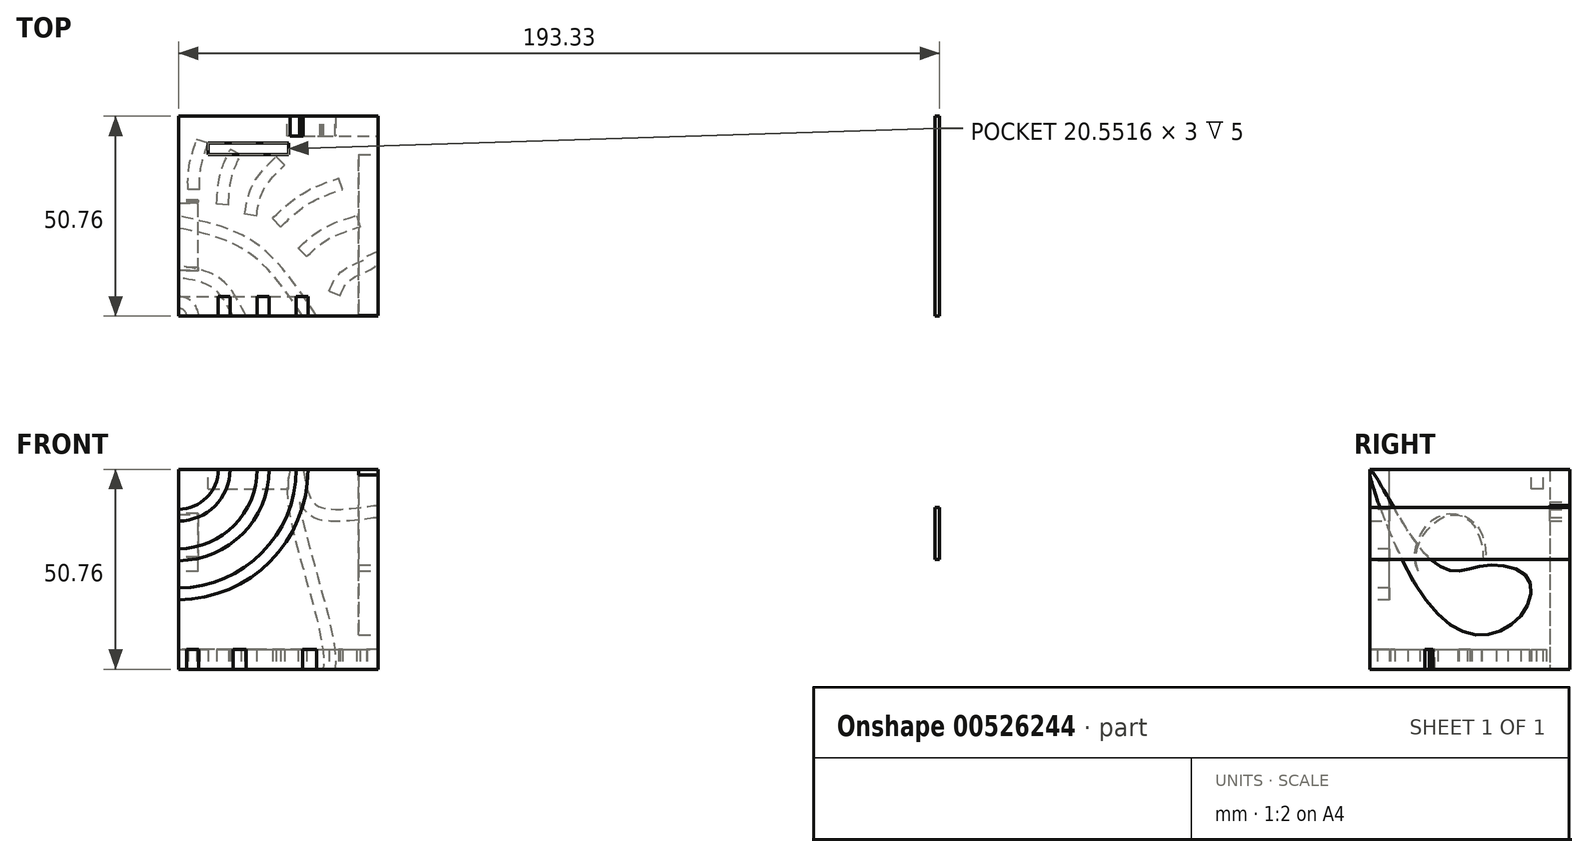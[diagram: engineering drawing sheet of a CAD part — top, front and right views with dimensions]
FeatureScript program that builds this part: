
annotation { "Feature Type Name" : "Feature", "Feature Type Description" : "" }
export const myFeature = defineFeature(function(context is Context, id is Id, definition is map)
    precondition{}
    {
        {
            var Q0;
            Q0=qCreatedBy(makeId("Front.planeOp"),FACE);
            var sketch = newSketch(context, id + "F0", { "sketchPlane" : qUnion([Q0])});
            skLineSegment(sketch, "E0.bottom", {"start": v(-59.56, 56.89) * mm, "end": v(-8.8, 56.89) * mm});
            skLineSegment(sketch, "E0.top", {"start": v(-59.56, 6.13) * mm, "end": v(-8.8, 6.13) * mm});
            skLineSegment(sketch, "E0.left", {"start": v(-59.56, 56.89) * mm, "end": v(-59.56, 6.13) * mm});
            skLineSegment(sketch, "E0.right", {"start": v(-8.8, 56.89) * mm, "end": v(-8.8, 6.13) * mm});
            skLineSegment(sketch, "E1.bottom", {"start": v(133.77, 47.2) * mm, "end": v(132.63, 47.2) * mm});
            skLineSegment(sketch, "E1.top", {"start": v(133.77, 38.64) * mm, "end": v(132.63, 38.64) * mm});
            skLineSegment(sketch, "E1.left", {"start": v(133.77, 47.2) * mm, "end": v(133.77, 38.64) * mm});
            skLineSegment(sketch, "E1.right", {"start": v(132.63, 47.2) * mm, "end": v(132.63, 38.64) * mm});
            skLineSegment(sketch, "E2.bottom", {"start": v(132.63, 38.64) * mm, "end": v(133.77, 38.64) * mm});
            skLineSegment(sketch, "E2.top", {"start": v(132.63, 34.08) * mm, "end": v(133.77, 34.08) * mm});
            skLineSegment(sketch, "E2.left", {"start": v(132.63, 38.64) * mm, "end": v(132.63, 34.08) * mm});
            skLineSegment(sketch, "E2.right", {"start": v(133.77, 38.64) * mm, "end": v(133.77, 34.08) * mm});
            skSolve(sketch);
        }
        {
            var Q0;
            Q0=qSketchRegion(id+"F0",true);
            extrude(context, id + "F1", {"entities" : qUnion([Q0]), "depth" : 50.76 * mm, "offsetDistance" : 25 * mm});
        }
        {
            var Q0;
            Q0=makeQuery(id+"F1.opExtrude","CAP_FACE",FACE,{"disambiguationData":[OSD([sQuery(id+"F0.wireOp",EDGE,"E0.bottom"),sQuery(id+"F0.wireOp",EDGE,"E0.top"),sQuery(id+"F0.wireOp",EDGE,"E0.left"),sQuery(id+"F0.wireOp",EDGE,"E0.right")])],"isStart":false});
            var sketch = newSketch(context, id + "F2", { "sketchPlane" : qUnion([Q0])});
            skSolve(sketch);
        }
        {
            var Q0;
            Q0=makeQuery(id+"F2.imprint","IMPRINT",FACE,{"disambiguationData":[TD([[makeQuery(id+"F2.imprint","IMPRINT",EDGE,{"derivedFrom":makeQuery(id+"F1.opExtrude","CAP_EDGE",EDGE,{"disambiguationData":[OSD([sQuery(id+"F0.wireOp",EDGE,"E0.bottom")])],"isStart":false})}),-1.0]])]});
            var sketch = newSketch(context, id + "F3", { "sketchPlane" : qUnion([Q0])});
            skArc(sketch, "E3", {"start": v(-59.55, 46.8) * mm, "mid": v(-52.35, 49.82) * mm, "end": v(-49.46, 57.07) * mm});
            skArc(sketch, "E4.0", {"start": v(-59.55, 43.8) * mm, "mid": v(-50.21, 47.72) * mm, "end": v(-46.46, 57.13) * mm});
            skLineSegment(sketch, "E5", {"start": v(-59.55, 46.8) * mm, "end": v(-64.57, 43.8) * mm});
            skLineSegment(sketch, "E6", {"start": v(-64.57, 43.8) * mm, "end": v(-59.55, 43.8) * mm});
            skLineSegment(sketch, "E7", {"start": v(-49.46, 57.07) * mm, "end": v(-46.79, 60.64) * mm});
            skLineSegment(sketch, "E8", {"start": v(-46.79, 60.64) * mm, "end": v(-46.46, 57.13) * mm});
            skSolve(sketch);
        }
        {
            var Q0;
            Q0=makeQuery(id+"F2.imprint","IMPRINT",FACE,{"disambiguationData":[TD([[makeQuery(id+"F2.imprint","IMPRINT",EDGE,{"derivedFrom":makeQuery(id+"F1.opExtrude","CAP_EDGE",EDGE,{"disambiguationData":[OSD([sQuery(id+"F0.wireOp",EDGE,"E0.bottom")])],"isStart":false})}),-1.0]])]});
            var sketch = newSketch(context, id + "F4", { "sketchPlane" : qUnion([Q0])});
            skArc(sketch, "E9", {"start": v(-59.74, 36.71) * mm, "mid": v(-45.4, 42.69) * mm, "end": v(-39.56, 57.08) * mm});
            skArc(sketch, "E10", {"start": v(-59.74, 26.81) * mm, "mid": v(-38.47, 35.62) * mm, "end": v(-29.66, 56.9) * mm});
            skArc(sketch, "E11.0", {"start": v(-59.74, 23.81) * mm, "mid": v(-36.35, 33.5) * mm, "end": v(-26.66, 56.9) * mm});
            skArc(sketch, "E12.0", {"start": v(-59.74, 33.71) * mm, "mid": v(-43.27, 40.58) * mm, "end": v(-36.56, 57.1) * mm});
            skLineSegment(sketch, "E13", {"start": v(-59.74, 36.71) * mm, "end": v(-64.36, 33.9) * mm});
            skLineSegment(sketch, "E14", {"start": v(-64.36, 33.9) * mm, "end": v(-59.74, 33.71) * mm});
            skLineSegment(sketch, "E15", {"start": v(-59.74, 26.81) * mm, "end": v(-63.86, 25.48) * mm});
            skLineSegment(sketch, "E16", {"start": v(-63.86, 25.48) * mm, "end": v(-59.74, 23.81) * mm});
            skLineSegment(sketch, "E17", {"start": v(-39.56, 57.08) * mm, "end": v(-36.56, 63.03) * mm});
            skLineSegment(sketch, "E18", {"start": v(-36.56, 63.03) * mm, "end": v(-36.56, 57.1) * mm});
            skLineSegment(sketch, "E19", {"start": v(-29.66, 56.9) * mm, "end": v(-26.66, 64.32) * mm});
            skLineSegment(sketch, "E20", {"start": v(-26.66, 64.32) * mm, "end": v(-26.66, 56.9) * mm});
            skSolve(sketch);
        }
        {
            var Q0;
            Q0=makeQuery(id+"F1.opExtrude","SWEPT_FACE",FACE,{"disambiguationData":[OSD([sQuery(id+"F0.wireOp",EDGE,"E0.bottom")])]});
            var sketch = newSketch(context, id + "F5", { "sketchPlane" : qUnion([Q0])});
            skLineSegment(sketch, "E21", {"start": v(-52.08, -6.76) * mm, "end": v(-31.52, -6.76) * mm});
            skLineSegment(sketch, "E22.0", {"start": v(-52.08, -9.76) * mm, "end": v(-31.52, -9.76) * mm});
            skLineSegment(sketch, "E23", {"start": v(-52.08, -6.76) * mm, "end": v(-52.08, -9.76) * mm});
            skLineSegment(sketch, "E24", {"start": v(-31.52, -6.76) * mm, "end": v(-31.52, -9.76) * mm});
            skSolve(sketch);
        }
        {
            var Q0;
            Q0=qCreatedBy(makeId("Front.planeOp"),FACE);
            var sketch = newSketch(context, id + "F6", { "sketchPlane" : qUnion([Q0])});
            skFitSpline(sketch, "E25", {"points": [v(-31.15, 57.08) * mm, v(-31.71, 47.74) * mm, v(-23.3, 13.73) * mm, v(-22.93, 6.26) * mm, v(-23.12, 6.26) * mm], "startDerivative": vector(-6.9, -29.17) * mm, "endDerivative": vector(-5.47, 1.83) * mm});
            skFitSpline(sketch, "E26.0", {"points": [v(-28.23, 56.39) * mm, v(-28.38, 55.78) * mm, v(-28.64, 54.64) * mm, v(-28.87, 53.23) * mm, v(-28.96, 51.94) * mm, v(-28.97, 50.87) * mm, v(-28.91, 49.65) * mm, v(-28.8, 48.5) * mm, v(-28.64, 47.46) * mm, v(-28.46, 46.35) * mm, v(-28.17, 44.85) * mm, v(-27.73, 42.87) * mm, v(-27.05, 40.06) * mm, v(-26.06, 36.27) * mm, v(-24.73, 31.48) * mm, v(-23.37, 26.65) * mm, v(-22.3, 22.72) * mm, v(-21.54, 19.72) * mm, v(-21.03, 17.56) * mm, v(-20.58, 15.52) * mm, v(-20.22, 13.6) * mm, v(-19.96, 11.83) * mm, v(-19.81, 10.52) * mm, v(-19.74, 9.56) * mm, v(-19.7, 8.9) * mm, v(-19.68, 8.27) * mm, v(-19.68, 7.7) * mm, v(-19.7, 7.16) * mm, v(-19.73, 6.74) * mm, v(-19.77, 6.4) * mm, v(-19.8, 6.15) * mm, v(-19.87, 5.87) * mm, v(-19.95, 5.57) * mm, v(-20.07, 5.22) * mm, v(-20.25, 4.84) * mm, v(-20.5, 4.48) * mm, v(-20.72, 4.22) * mm, v(-20.95, 4) * mm, v(-21.23, 3.78) * mm, v(-21.64, 3.53) * mm, v(-22.17, 3.33) * mm, v(-22.69, 3.24) * mm, v(-23.13, 3.23) * mm, v(-23.6, 3.28) * mm, v(-23.95, 3.37) * mm, v(-24.05, 3.4) * mm, v(-24.07, 3.41) * mm]});
            skLineSegment(sketch, "E27", {"start": v(-31.15, 57.08) * mm, "end": v(-27.86, 64.5) * mm});
            skLineSegment(sketch, "E28", {"start": v(-27.86, 64.5) * mm, "end": v(-28.23, 56.39) * mm});
            skLineSegment(sketch, "E29", {"start": v(-33.73, 3.41) * mm, "end": v(-24.07, 3.41) * mm});
            skLineSegment(sketch, "E30", {"start": v(-23.12, 6.26) * mm, "end": v(-33.73, 3.41) * mm});
            skSolve(sketch);
        }
        {
            var Q0;
            Q0=makeQuery(id+"F1.opExtrude","CAP_FACE",FACE,{"disambiguationData":[OSD([sQuery(id+"F0.wireOp",EDGE,"E0.bottom"),sQuery(id+"F0.wireOp",EDGE,"E0.top"),sQuery(id+"F0.wireOp",EDGE,"E0.left"),sQuery(id+"F0.wireOp",EDGE,"E0.right")])],"isStart":true});
            var sketch = newSketch(context, id + "F7", { "sketchPlane" : qUnion([Q0])});
            skFitSpline(sketch, "E31", {"points": [v(30.94, 56.89) * mm, v(24.23, 44.4) * mm, v(8.8, 44.68) * mm, v(8.8, 44.4) * mm], "startDerivative": vector(-5.85, -35.55) * mm, "endDerivative": vector(2.46, -5.15) * mm});
            skFitSpline(sketch, "E32.0", {"points": [v(27.98, 57.37) * mm, v(27.85, 56.63) * mm, v(27.62, 55.18) * mm, v(27.22, 53.16) * mm, v(26.73, 51.37) * mm, v(26.14, 49.87) * mm, v(25.45, 48.74) * mm, v(24.81, 48.07) * mm, v(24.22, 47.66) * mm, v(23.7, 47.4) * mm, v(23.08, 47.17) * mm, v(22.28, 46.99) * mm, v(21.33, 46.86) * mm, v(19.92, 46.77) * mm, v(18.36, 46.79) * mm, v(16.75, 46.9) * mm, v(15.56, 47) * mm, v(14.4, 47.14) * mm, v(13.28, 47.28) * mm, v(12.42, 47.4) * mm, v(11.77, 47.48) * mm, v(11.31, 47.54) * mm, v(10.87, 47.6) * mm, v(10.46, 47.65) * mm, v(10.07, 47.69) * mm, v(9.7, 47.72) * mm, v(9.37, 47.73) * mm, v(9.1, 47.74) * mm, v(8.87, 47.73) * mm, v(8.6, 47.7) * mm, v(8.33, 47.66) * mm, v(8.06, 47.6) * mm, v(7.82, 47.52) * mm, v(7.53, 47.4) * mm, v(7.2, 47.22) * mm, v(6.83, 46.96) * mm, v(6.47, 46.6) * mm, v(6.16, 46.17) * mm, v(5.93, 45.68) * mm, v(5.8, 45.2) * mm, v(5.72, 44.62) * mm, v(5.77, 44.05) * mm, v(5.89, 43.61) * mm, v(6, 43.34) * mm, v(6.07, 43.18) * mm, v(6.1, 43.12) * mm, v(6.1, 43.1) * mm]});
            skLineSegment(sketch, "E33", {"start": v(27.98, 57.37) * mm, "end": v(30.94, 56.89) * mm});
            skLineSegment(sketch, "E34", {"start": v(8.8, 44.68) * mm, "end": v(6.1, 43.1) * mm});
            skSolve(sketch);
        }
        {
            var Q0;
            Q0=makeQuery(id+"F1.opExtrude","SWEPT_FACE",FACE,{"disambiguationData":[OSD([sQuery(id+"F0.wireOp",EDGE,"E0.top")])]});
            var sketch = newSketch(context, id + "F8", { "sketchPlane" : qUnion([Q0])});
            skFitSpline(sketch, "E35", {"points": [v(-42.36, 50.76) * mm, v(-49.09, 41.2) * mm, v(-59.56, 38.02) * mm], "startDerivative": vector(-11.18, -21.96) * mm, "endDerivative": vector(-23.28, -3.42) * mm});
            skFitSpline(sketch, "E36", {"points": [v(-24.42, 50.76) * mm, v(-40.3, 32.04) * mm, v(-59.56, 25.38) * mm], "startDerivative": vector(-27.72, -41.47) * mm, "endDerivative": vector(-42.78, -8.78) * mm});
            skFitSpline(sketch, "E37", {"points": [v(-21.25, 44.37) * mm, v(-17.7, 39.14) * mm, v(-11.72, 35.97) * mm, v(-11.72, 35.6) * mm], "startDerivative": vector(5.24, -12.88) * mm, "endDerivative": vector(-1.53, -3.26) * mm});
            skFitSpline(sketch, "E38", {"points": [v(-27.04, 35.7) * mm, v(-21.62, 31.3) * mm, v(-13.4, 28.12) * mm], "startDerivative": vector(10.55, -10.16) * mm, "endDerivative": vector(16.6, -5.11) * mm});
            skFitSpline(sketch, "E39", {"points": [v(-33.58, 28.12) * mm, v(-26.67, 22.33) * mm, v(-17.89, 18.59) * mm], "startDerivative": vector(13.21, -12.83) * mm, "endDerivative": vector(18.15, -6.26) * mm});
            skFitSpline(sketch, "E40", {"points": [v(-39.75, 25.38) * mm, v(-37.88, 18.59) * mm, v(-32.65, 12.42) * mm], "startDerivative": vector(2.36, -14.58) * mm, "endDerivative": vector(11.73, -11.36) * mm});
            skFitSpline(sketch, "E41", {"points": [v(-46.84, 22.51) * mm, v(-45.91, 15.04) * mm, v(-43.67, 9.8) * mm], "startDerivative": vector(0.92, -14.7) * mm, "endDerivative": vector(5.54, -10.62) * mm});
            skFitSpline(sketch, "E42", {"points": [v(-54.13, 18.59) * mm, v(-53.94, 13.55) * mm, v(-52.08, 6.82) * mm], "startDerivative": vector(-0.3, -10.64) * mm, "endDerivative": vector(4.28, -12.84) * mm});
            skFitSpline(sketch, "E43.0", {"points": [v(-18.47, 45.5) * mm, v(-18.25, 44.97) * mm, v(-17.85, 44) * mm, v(-17.34, 43.05) * mm, v(-16.87, 42.42) * mm, v(-16.53, 42.06) * mm, v(-16.22, 41.78) * mm, v(-16, 41.61) * mm, v(-15.8, 41.48) * mm, v(-15.59, 41.33) * mm, v(-15.28, 41.14) * mm, v(-14.87, 40.91) * mm, v(-14.29, 40.6) * mm, v(-13.65, 40.3) * mm, v(-13.02, 40.01) * mm, v(-12.55, 39.8) * mm, v(-12.08, 39.6) * mm, v(-11.64, 39.39) * mm, v(-11.2, 39.18) * mm, v(-10.85, 39) * mm, v(-10.55, 38.83) * mm, v(-10.32, 38.68) * mm, v(-10.06, 38.5) * mm, v(-9.77, 38.27) * mm, v(-9.48, 37.98) * mm, v(-9.21, 37.63) * mm, v(-9.03, 37.32) * mm, v(-8.87, 36.98) * mm, v(-8.7, 36.48) * mm, v(-8.63, 35.82) * mm, v(-8.7, 35.15) * mm, v(-8.84, 34.7) * mm, v(-8.96, 34.42) * mm, v(-9, 34.33) * mm, v(-9, 34.32) * mm]});
            skFitSpline(sketch, "E44.0", {"points": [v(-29.12, 33.55) * mm, v(-28.68, 33.12) * mm, v(-27.78, 32.25) * mm, v(-26.54, 31.14) * mm, v(-25.45, 30.26) * mm, v(-24.59, 29.62) * mm, v(-23.66, 29) * mm, v(-22.67, 28.43) * mm, v(-21.65, 27.91) * mm, v(-20.27, 27.29) * mm, v(-18.51, 26.6) * mm, v(-16.38, 25.9) * mm, v(-14.98, 25.46) * mm, v(-14.28, 25.25) * mm]});
            skFitSpline(sketch, "E45.0", {"points": [v(-35.67, 25.97) * mm, v(-35.12, 25.43) * mm, v(-34, 24.34) * mm, v(-32.51, 22.98) * mm, v(-31.25, 21.91) * mm, v(-30.26, 21.14) * mm, v(-29.39, 20.51) * mm, v(-28.67, 20.04) * mm, v(-27.92, 19.57) * mm, v(-26.98, 19.04) * mm, v(-25.44, 18.26) * mm, v(-23.5, 17.42) * mm, v(-21.16, 16.54) * mm, v(-19.62, 16.01) * mm, v(-18.86, 15.75) * mm]});
            skFitSpline(sketch, "E46.0", {"points": [v(-42.7, 24.9) * mm, v(-42.6, 24.3) * mm, v(-42.4, 23.04) * mm, v(-42.06, 21.38) * mm, v(-41.69, 20.02) * mm, v(-41.34, 18.98) * mm, v(-40.99, 18.11) * mm, v(-40.65, 17.42) * mm, v(-40.29, 16.73) * mm, v(-39.79, 15.91) * mm, v(-39.13, 14.99) * mm, v(-38.44, 14.11) * mm, v(-37.47, 13) * mm, v(-36.22, 11.71) * mm, v(-35.22, 10.74) * mm, v(-34.73, 10.27) * mm]});
            skFitSpline(sketch, "E47.0", {"points": [v(-49.84, 22.33) * mm, v(-49.8, 21.71) * mm, v(-49.72, 20.47) * mm, v(-49.57, 18.57) * mm, v(-49.33, 16.67) * mm, v(-49.03, 15.1) * mm, v(-48.7, 13.84) * mm, v(-48.4, 12.95) * mm, v(-48.09, 12.1) * mm, v(-47.64, 11.02) * mm, v(-47.04, 9.78) * mm, v(-46.56, 8.86) * mm, v(-46.33, 8.42) * mm]});
            skFitSpline(sketch, "E48.0", {"points": [v(-57.13, 18.67) * mm, v(-57.14, 18.23) * mm, v(-57.17, 17.31) * mm, v(-57.17, 16.08) * mm, v(-57.12, 15.04) * mm, v(-57.06, 14.23) * mm, v(-56.96, 13.4) * mm, v(-56.77, 12.24) * mm, v(-56.46, 10.83) * mm, v(-55.99, 9.15) * mm, v(-55.46, 7.5) * mm, v(-55.1, 6.4) * mm, v(-54.92, 5.87) * mm]});
            skFitSpline(sketch, "E49.0", {"points": [v(-26.92, 52.43) * mm, v(-28.07, 50.7) * mm, v(-30.36, 47.27) * mm, v(-33.84, 42.47) * mm, v(-36.85, 38.96) * mm, v(-39.34, 36.56) * mm, v(-40.94, 35.26) * mm, v(-42.25, 34.34) * mm, v(-43.6, 33.5) * mm, v(-45.35, 32.55) * mm, v(-47.58, 31.6) * mm, v(-50.7, 30.5) * mm, v(-54.87, 29.4) * mm, v(-58.38, 28.68) * mm, v(-60.16, 28.32) * mm]});
            skFitSpline(sketch, "E50.0", {"points": [v(-45.03, 52.12) * mm, v(-45.5, 51.2) * mm, v(-46.41, 49.42) * mm, v(-47.56, 47.41) * mm, v(-48.51, 46.02) * mm, v(-49.24, 45.1) * mm, v(-49.86, 44.45) * mm, v(-50.36, 44) * mm, v(-50.74, 43.7) * mm, v(-51.13, 43.43) * mm, v(-51.69, 43.08) * mm, v(-52.45, 42.7) * mm, v(-53.48, 42.3) * mm, v(-55, 41.85) * mm, v(-57.14, 41.4) * mm, v(-59.03, 41.13) * mm, v(-60, 40.99) * mm]});
            skLineSegment(sketch, "E51", {"start": v(-45.03, 52.12) * mm, "end": v(-42.36, 50.76) * mm});
            skLineSegment(sketch, "E52", {"start": v(-60, 40.99) * mm, "end": v(-59.56, 38.02) * mm});
            skLineSegment(sketch, "E53", {"start": v(-63.89, 24.3) * mm, "end": v(-59.56, 25.38) * mm});
            skLineSegment(sketch, "E54", {"start": v(-59.56, 25.38) * mm, "end": v(-63.89, 24.3) * mm});
            skLineSegment(sketch, "E55", {"start": v(-26.92, 52.43) * mm, "end": v(-21.16, 57.8) * mm});
            skLineSegment(sketch, "E56", {"start": v(-21.16, 57.8) * mm, "end": v(-24.42, 50.76) * mm});
            skLineSegment(sketch, "E57", {"start": v(-14.28, 25.25) * mm, "end": v(-13.4, 28.12) * mm});
            skLineSegment(sketch, "E58", {"start": v(-27.04, 35.7) * mm, "end": v(-29.12, 33.55) * mm});
            skLineSegment(sketch, "E59", {"start": v(-35.67, 25.97) * mm, "end": v(-33.58, 28.12) * mm});
            skLineSegment(sketch, "E60", {"start": v(-17.89, 18.59) * mm, "end": v(-18.86, 15.75) * mm});
            skLineSegment(sketch, "E61", {"start": v(-32.65, 12.42) * mm, "end": v(-34.73, 10.27) * mm});
            skLineSegment(sketch, "E62", {"start": v(-39.75, 25.38) * mm, "end": v(-42.7, 24.9) * mm});
            skLineSegment(sketch, "E63", {"start": v(-46.84, 22.51) * mm, "end": v(-49.84, 22.33) * mm});
            skLineSegment(sketch, "E64", {"start": v(-43.67, 9.8) * mm, "end": v(-46.33, 8.42) * mm});
            skLineSegment(sketch, "E65", {"start": v(-54.13, 18.59) * mm, "end": v(-57.13, 18.67) * mm});
            skLineSegment(sketch, "E66", {"start": v(-52.08, 6.82) * mm, "end": v(-54.92, 5.87) * mm});
            skLineSegment(sketch, "E67", {"start": v(-9, 34.32) * mm, "end": v(-11.72, 35.6) * mm});
            skLineSegment(sketch, "E68", {"start": v(-60.16, 28.32) * mm, "end": v(-63.89, 24.3) * mm});
            skLineSegment(sketch, "E69", {"start": v(-21.25, 44.37) * mm, "end": v(-18.47, 45.5) * mm});
            skSolve(sketch);
        }
        {
            var Q0;
            {var subQ0=sQuery(id+"F8.wireOp",EDGE,"E35");Q0=makeQuery(id+"F8.imprint","IMPRINT",FACE,{"disambiguationData":[TD([[makeQuery(id+"F8.imprint","IMPRINT",EDGE,{"derivedFrom":subQ0}),-1.0]])]});}
            var sketch = newSketch(context, id + "F9", { "sketchPlane" : qUnion([Q0])});
            skArc(sketch, "E70", {"start": v(-59.68, 45.81) * mm, "mid": v(-56.04, 47.21) * mm, "end": v(-54.45, 50.78) * mm});
            skArc(sketch, "E71.0", {"start": v(-59.6, 48.81) * mm, "mid": v(-58.1, 49.39) * mm, "end": v(-57.45, 50.86) * mm});
            skLineSegment(sketch, "E72", {"start": v(-57.45, 50.86) * mm, "end": v(-56.02, 53.41) * mm});
            skLineSegment(sketch, "E73", {"start": v(-56.02, 53.41) * mm, "end": v(-54.45, 50.78) * mm});
            skLineSegment(sketch, "E74", {"start": v(-59.6, 48.81) * mm, "end": v(-62.29, 47.39) * mm});
            skLineSegment(sketch, "E75", {"start": v(-62.29, 47.39) * mm, "end": v(-59.68, 45.81) * mm});
            skSolve(sketch);
        }
        {
            var Q0;
            Q0=makeQuery(id+"F1.opExtrude","SWEPT_FACE",FACE,{"disambiguationData":[OSD([sQuery(id+"F0.wireOp",EDGE,"E0.right")])]});
            var sketch = newSketch(context, id + "F10", { "sketchPlane" : qUnion([Q0])});
            skFitSpline(sketch, "E76", {"points": [v(-50.76, 56.89) * mm, v(-39.8, 28.68) * mm, v(-23.35, 14.85) * mm, v(-12.33, 19.9) * mm, v(-10.46, 29.05) * mm, v(-20.36, 32.6) * mm, v(-29.15, 31.1) * mm, v(-39.23, 38.58) * mm, v(-50.76, 56.89) * mm]});
            skFitSpline(sketch, "E77.0", {"points": [v(-51.05, 59.9) * mm, v(-51.6, 59.79) * mm, v(-52.13, 59.58) * mm, v(-52.6, 59.28) * mm, v(-52.98, 58.94) * mm, v(-53.35, 58.49) * mm, v(-53.62, 57.97) * mm, v(-53.77, 57.5) * mm, v(-53.85, 57.12) * mm, v(-53.88, 56.82) * mm, v(-53.89, 56.56) * mm, v(-53.88, 56.25) * mm, v(-53.86, 55.9) * mm, v(-53.8, 55.5) * mm, v(-53.74, 55.09) * mm, v(-53.65, 54.66) * mm, v(-53.55, 54.22) * mm, v(-53.4, 53.59) * mm, v(-53.18, 52.74) * mm, v(-52.85, 51.6) * mm, v(-52.47, 50.38) * mm, v(-52.03, 49.05) * mm, v(-51.55, 47.64) * mm, v(-51.02, 46.15) * mm, v(-50.25, 44.09) * mm, v(-49.19, 41.38) * mm, v(-47.78, 38) * mm, v(-46.26, 34.6) * mm, v(-44.64, 31.28) * mm, v(-43.23, 28.63) * mm, v(-42.08, 26.63) * mm, v(-40.91, 24.73) * mm, v(-39.43, 22.53) * mm, v(-37, 19.4) * mm, v(-33.84, 16.16) * mm, v(-29.79, 13.41) * mm, v(-26.2, 12.14) * mm, v(-23.23, 11.79) * mm, v(-21.03, 11.86) * mm, v(-18.9, 12.25) * mm, v(-16.16, 13.14) * mm, v(-13.65, 14.53) * mm, v(-11.45, 16.36) * mm, v(-10, 17.94) * mm, v(-8.75, 19.7) * mm, v(-7.76, 21.59) * mm, v(-7.06, 23.58) * mm, v(-6.7, 25.67) * mm, v(-6.77, 27.47) * mm, v(-7.1, 28.92) * mm, v(-7.45, 29.8) * mm, v(-7.82, 30.5) * mm, v(-8.24, 31.15) * mm, v(-8.84, 31.89) * mm, v(-9.66, 32.64) * mm, v(-10.82, 33.5) * mm, v(-12.4, 34.32) * mm, v(-14.39, 35) * mm, v(-16.45, 35.44) * mm, v(-18.18, 35.61) * mm, v(-19.55, 35.64) * mm, v(-20.57, 35.6) * mm, v(-21.56, 35.51) * mm, v(-22.8, 35.34) * mm, v(-24.21, 35.04) * mm, v(-25.7, 34.66) * mm, v(-27, 34.34) * mm, v(-27.9, 34.17) * mm, v(-28.52, 34.1) * mm, v(-28.93, 34.1) * mm, v(-29.31, 34.12) * mm, v(-29.7, 34.18) * mm, v(-30.1, 34.27) * mm, v(-30.66, 34.46) * mm, v(-31.41, 34.82) * mm, v(-32.44, 35.51) * mm, v(-33.59, 36.5) * mm, v(-34.84, 37.81) * mm, v(-35.96, 39.19) * mm, v(-36.9, 40.46) * mm, v(-37.88, 41.87) * mm, v(-39.14, 43.81) * mm, v(-40.67, 46.32) * mm, v(-41.93, 48.46) * mm, v(-42.9, 50.13) * mm, v(-43.6, 51.35) * mm, v(-44.28, 52.53) * mm, v(-44.92, 53.65) * mm, v(-45.53, 54.7) * mm, v(-46.1, 55.66) * mm, v(-46.54, 56.38) * mm, v(-46.88, 56.91) * mm, v(-47.12, 57.28) * mm, v(-47.35, 57.63) * mm, v(-47.58, 57.96) * mm, v(-47.82, 58.27) * mm, v(-48.03, 58.53) * mm, v(-48.23, 58.74) * mm, v(-48.4, 58.91) * mm, v(-48.6, 59.1) * mm, v(-48.86, 59.3) * mm, v(-49.21, 59.52) * mm, v(-49.64, 59.71) * mm, v(-50.12, 59.84) * mm, v(-50.55, 59.9) * mm, v(-51.05, 59.9) * mm, v(-51.6, 59.79) * mm, v(-52.13, 59.58) * mm, v(-51.05, 59.9) * mm]});
            skSolve(sketch);
        }
        {
            var Q0;
            Q0 = qSketchRegion(id + "F4", true);
            extrude(context, id + "F11", {"entities" : qUnion([Q0]), "operationType" : NewBodyOperationType.REMOVE, "oppositeDirection" : true, "depth" : 5 * mm, "offsetDistance" : 25 * mm});
        }
        {
            var Q0;
            Q0 = qSketchRegion(id + "F3", true);
            extrude(context, id + "F12", {"entities" : qUnion([Q0]), "operationType" : NewBodyOperationType.REMOVE, "oppositeDirection" : true, "depth" : 5 * mm, "offsetDistance" : 25 * mm});
        }
        {
            var Q0;
            Q0 = qSketchRegion(id + "F5", true);
            extrude(context, id + "F13", {"entities" : qUnion([Q0]), "operationType" : NewBodyOperationType.REMOVE, "oppositeDirection" : true, "depth" : 5 * mm, "offsetDistance" : 25 * mm});
        }
        {
            var Q0;
            Q0 = qSketchRegion(id + "F7", true);
            extrude(context, id + "F14", {"entities" : qUnion([Q0]), "operationType" : NewBodyOperationType.REMOVE, "oppositeDirection" : true, "depth" : 5 * mm, "offsetDistance" : 25 * mm});
        }
        {
            var Q0;
            Q0 = qSketchRegion(id + "F8", true);
            extrude(context, id + "F15", {"entities" : qUnion([Q0]), "operationType" : NewBodyOperationType.REMOVE, "oppositeDirection" : true, "depth" : 5 * mm, "offsetDistance" : 25 * mm});
        }
        {
            var Q0;
            Q0=makeQuery(id+"F9.imprint","IMPRINT",FACE,{"disambiguationData":[TD([[makeQuery(id+"F9.imprint","IMPRINT",EDGE,{"derivedFrom":sQuery(id+"F9.wireOp",EDGE,"E70")}),1.0]])]});
            extrude(context, id + "F16", {"entities" : qUnion([Q0]), "operationType" : NewBodyOperationType.REMOVE, "oppositeDirection" : true, "depth" : 5 * mm, "offsetDistance" : 25 * mm});
        }
        {
            var Q0;
            Q0 = qSketchRegion(id + "F6", true);
            extrude(context, id + "F17", {"entities" : qUnion([Q0]), "operationType" : NewBodyOperationType.REMOVE, "oppositeDirection" : true, "depth" : 5 * mm, "offsetDistance" : 25 * mm});
        }
        {
            var Q0;
            Q0 = qSketchRegion(id + "F6", true);
            extrude(context, id + "F18", {"entities" : qUnion([Q0]), "operationType" : NewBodyOperationType.REMOVE, "oppositeDirection" : true, "depth" : 5 * mm, "offsetDistance" : 25 * mm});
        }
        {
            var Q0;
            Q0 = qSketchRegion(id + "F10", true);
            extrude(context, id + "F19", {"entities" : qUnion([Q0]), "operationType" : NewBodyOperationType.REMOVE, "oppositeDirection" : true, "depth" : 5 * mm, "offsetDistance" : 25 * mm});
        }
        {
            var Q0;
            Q0 = qSketchRegion(id + "F6", true);
            extrude(context, id + "F20", {"entities" : qUnion([Q0]), "operationType" : NewBodyOperationType.REMOVE, "oppositeDirection" : true, "depth" : 5 * mm, "offsetDistance" : 25 * mm});
        }
        {
            var Q0;
            Q0=makeQuery(id+"F1.opExtrude","SWEPT_FACE",FACE,{"disambiguationData":[OSD([sQuery(id+"F0.wireOp",EDGE,"E0.left")])]});
            var sketch = newSketch(context, id + "F21", { "sketchPlane" : qUnion([Q0])});
            skFitSpline(sketch, "E78", {"points": [v(0, 56.89) * mm, v(8.38, 29.32) * mm, v(30.16, 16.2) * mm, v(43, 27.37) * mm, v(39.1, 45.8) * mm, v(19.83, 46.64) * mm, v(17.31, 34.35) * mm, v(27.65, 27.09) * mm, v(36.02, 34.63) * mm, v(28.2, 42.17) * mm, v(25.13, 34.63) * mm, v(25.7, 34.9) * mm], "startDerivative": vector(30.83, -221.9) * mm, "endDerivative": vector(34.39, 34.73) * mm});
            skFitSpline(sketch, "E79.0", {"points": [v(-2.97, 56.47) * mm, v(-2.65, 54.16) * mm, v(-2, 49.5) * mm, v(-0.65, 42.46) * mm, v(1.1, 36.7) * mm, v(3.09, 32.24) * mm, v(4.6, 29.53) * mm, v(6.02, 27.43) * mm, v(7.56, 25.38) * mm, v(9.7, 22.97) * mm, v(12.53, 20.33) * mm, v(15.58, 18) * mm, v(18.8, 16.05) * mm, v(22.13, 14.52) * mm, v(24.98, 13.66) * mm, v(27.28, 13.28) * mm, v(29, 13.15) * mm, v(30.74, 13.2) * mm, v(32.43, 13.45) * mm, v(34.06, 13.87) * mm, v(36.13, 14.66) * mm, v(38.52, 16.03) * mm, v(41.01, 18.17) * mm, v(43.1, 20.73) * mm, v(44.8, 23.61) * mm, v(46.05, 26.77) * mm, v(46.85, 30.12) * mm, v(47.16, 33.55) * mm, v(46.97, 37) * mm, v(46.25, 40.37) * mm, v(45.14, 43.03) * mm, v(43.93, 45.01) * mm, v(42.84, 46.4) * mm, v(41.59, 47.67) * mm, v(40.15, 48.8) * mm, v(38.6, 49.73) * mm, v(36.43, 50.76) * mm, v(33.55, 51.65) * mm, v(29.96, 52.14) * mm, v(26.38, 52.1) * mm, v(23.51, 51.58) * mm, v(21.34, 50.88) * mm, v(19.79, 50.18) * mm, v(18.58, 49.46) * mm, v(17.67, 48.77) * mm, v(16.84, 48.03) * mm, v(15.91, 47.01) * mm, v(14.7, 45.23) * mm, v(13.71, 42.8) * mm, v(13.25, 39.75) * mm, v(13.44, 36.69) * mm, v(14.1, 34.22) * mm, v(14.9, 32.34) * mm, v(15.89, 30.56) * mm, v(17.42, 28.55) * mm, v(19.67, 26.53) * mm, v(21.86, 25.27) * mm, v(23.78, 24.56) * mm, v(25.28, 24.21) * mm, v(26.84, 24.05) * mm, v(28.45, 24.1) * mm, v(30.02, 24.37) * mm, v(32.04, 24.97) * mm, v(34.4, 26.16) * mm, v(36.4, 27.9) * mm, v(37.7, 29.63) * mm, v(38.46, 31.1) * mm, v(38.87, 32.47) * mm, v(39.02, 33.63) * mm, v(39.05, 34.52) * mm, v(38.97, 35.42) * mm, v(38.82, 36.29) * mm, v(38.6, 37.13) * mm, v(38.2, 38.2) * mm, v(37.59, 39.47) * mm, v(36.67, 40.88) * mm, v(35.61, 42.16) * mm, v(34.42, 43.3) * mm, v(33.1, 44.25) * mm, v(31.61, 45) * mm, v(30.2, 45.37) * mm, v(28.94, 45.41) * mm, v(28.12, 45.3) * mm, v(27.47, 45.1) * mm, v(26.99, 44.92) * mm, v(26.53, 44.68) * mm, v(25.97, 44.33) * mm, v(25.37, 43.83) * mm, v(24.6, 42.98) * mm, v(23.85, 41.85) * mm, v(23.3, 40.7) * mm, v(22.96, 39.79) * mm, v(22.73, 39.1) * mm, v(22.54, 38.44) * mm, v(22.38, 37.79) * mm, v(22.25, 37.16) * mm, v(22.15, 36.56) * mm, v(22.1, 36.09) * mm, v(22.06, 35.72) * mm, v(22.05, 35.44) * mm, v(22.04, 35.16) * mm, v(22.05, 34.87) * mm, v(22.07, 34.55) * mm, v(22.13, 34.19) * mm, v(22.23, 33.8) * mm, v(22.39, 33.4) * mm, v(22.59, 33.02) * mm, v(22.9, 32.6) * mm, v(23.36, 32.17) * mm, v(23.95, 31.81) * mm, v(24.62, 31.6) * mm, v(25.26, 31.55) * mm, v(25.8, 31.6) * mm, v(26.21, 31.72) * mm, v(26.65, 31.89) * mm, v(27.01, 32.1) * mm, v(27.3, 32.3) * mm, v(27.5, 32.48) * mm, v(27.64, 32.61) * mm, v(27.75, 32.72) * mm, v(27.8, 32.77) * mm, v(27.82, 32.8) * mm]});
            skFitSpline(sketch, "E80", {"points": [v(31.72, 24.93) * mm, v(38.82, 31.84) * mm, v(37.98, 40.21) * mm, v(31.72, 45.52) * mm, v(23.18, 42.17) * mm, v(21.5, 34.63) * mm, v(21.78, 34.63) * mm], "startDerivative": vector(43.36, 30) * mm, "endDerivative": vector(8.8, 4.02) * mm});
            skLineSegment(sketch, "E81", {"start": v(25.7, 34.9) * mm, "end": v(21.78, 34.63) * mm});
            skLineSegment(sketch, "E82", {"start": v(-2.97, 56.47) * mm, "end": v(-2.97, 62.55) * mm});
            skLineSegment(sketch, "E83", {"start": v(-2.97, 62.55) * mm, "end": v(0, 56.89) * mm});
            skSolve(sketch);
        }
        {
            var Q0;
            {var subQ0=sQuery(id+"F21.wireOp",EDGE,"E82");Q0=makeQuery(id+"F21.imprint","IMPRINT",FACE,{"disambiguationData":[TD([[makeQuery(id+"F21.imprint","IMPRINT",EDGE,{"derivedFrom":subQ0}),-1.0]])]});}
            var Q1;
            {var subQ13=sQuery(id+"F21.wireOp",EDGE,"E80");Q1=makeQuery(id+"F21.imprint","IMPRINT",FACE,{"disambiguationData":[TD([[makeQuery(id+"F21.imprint","IMPRINT",EDGE,{"derivedFrom":subQ13}),1.0]])]});}
            extrude(context, id + "F22", {"entities" : qUnion([Q0, Q1]), "operationType" : NewBodyOperationType.REMOVE, "oppositeDirection" : true, "depth" : 5 * mm, "offsetDistance" : 25 * mm});
        }
        {
            var Q0;
            Q0 = qSketchRegion(id + "F6", true);
            extrude(context, id + "F23", {"entities" : qUnion([Q0]), "operationType" : NewBodyOperationType.REMOVE, "oppositeDirection" : true, "depth" : 5 * mm, "offsetDistance" : 25 * mm});
        }
        {
            var Q0;
            Q0 = qSketchRegion(id + "F6", true);
            extrude(context, id + "F24", {"entities" : qUnion([Q0]), "operationType" : NewBodyOperationType.REMOVE, "oppositeDirection" : true, "depth" : 5 * mm, "offsetDistance" : 25 * mm});
        }
        {
            var Q0;
            Q0 = qSketchRegion(id + "F6", true);
            extrude(context, id + "F25", {"entities" : qUnion([Q0]), "operationType" : NewBodyOperationType.REMOVE, "oppositeDirection" : true, "depth" : 5 * mm, "offsetDistance" : 25 * mm});
        }
        {
            var Q0;
            Q0 = qSketchRegion(id + "F6", true);
            extrude(context, id + "F26", {"entities" : qUnion([Q0]), "operationType" : NewBodyOperationType.REMOVE, "oppositeDirection" : true, "depth" : 5 * mm, "offsetDistance" : 25 * mm});
        }
        {
            var Q0;
            Q0 = qSketchRegion(id + "F6", true);
            extrude(context, id + "F27", {"entities" : qUnion([Q0]), "operationType" : NewBodyOperationType.REMOVE, "oppositeDirection" : true, "depth" : 25 * mm, "offsetDistance" : 25 * mm});
        }
        {
            var Q0;
            Q0 = qSketchRegion(id + "F6", true);
            extrude(context, id + "F28", {"entities" : qUnion([Q0]), "operationType" : NewBodyOperationType.REMOVE, "depth" : 5 * mm, "offsetDistance" : 25 * mm});
        }
    });
